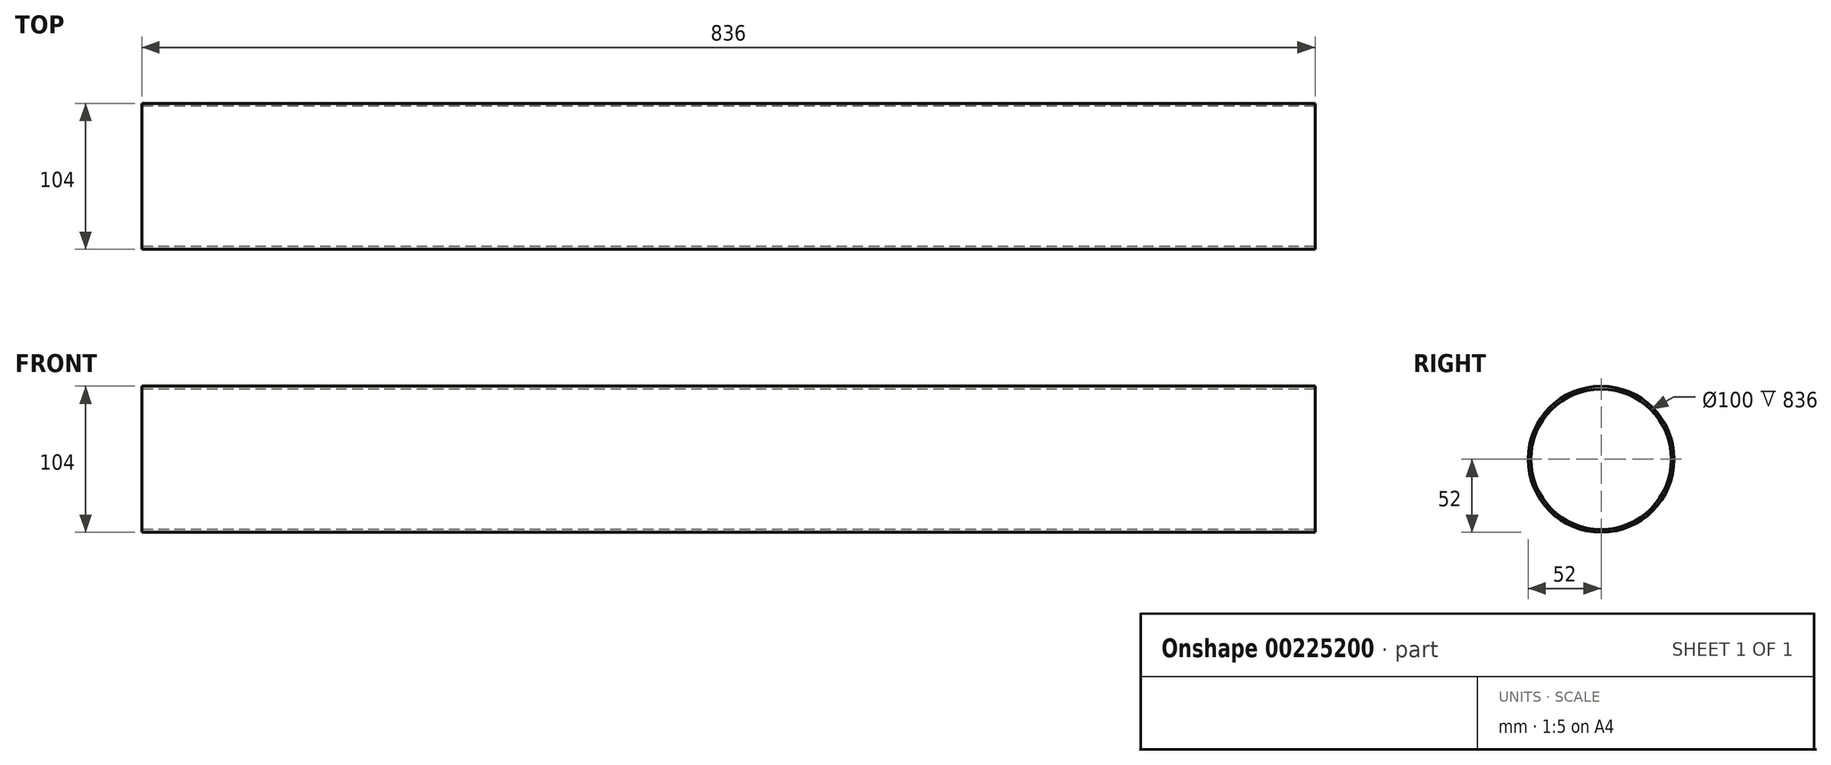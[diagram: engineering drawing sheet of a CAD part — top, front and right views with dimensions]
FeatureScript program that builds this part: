
annotation { "Feature Type Name" : "Feature", "Feature Type Description" : "" }
export const myFeature = defineFeature(function(context is Context, id is Id, definition is map)
    precondition{}
    {
        {
            var Q0;
            Q0=qCreatedBy(makeId("Right.planeOp"),FACE);
            var sketch = newSketch(context, id + "F0", { "sketchPlane" : qUnion([Q0])});
            skCircle(sketch, "E0", {"center": v(0, 0) * mm, "radius": 50 * mm});
            skCircle(sketch, "E1", {"center": v(0, 0) * mm, "radius": 52 * mm});
            skSolve(sketch);
        }
        {
            var Q0;
            Q0=makeQuery(id+"F0.imprint","IMPRINT",FACE,{"disambiguationData":[TD([[makeQuery(id+"F0.imprint","IMPRINT",EDGE,{"derivedFrom":sQuery(id+"F0.wireOp",EDGE,"E0")}),-1.0]])]});
            extrude(context, id + "F1", {"entities" : qUnion([Q0]), "depth" : 836 * mm});
        }
    });
